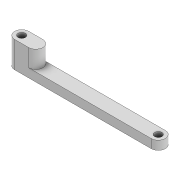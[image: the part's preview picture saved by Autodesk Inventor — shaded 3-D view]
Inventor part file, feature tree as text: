
AUTODESK INVENTOR PART (.ipt)
format: ipt  version: 2022 (Build 260153000, 153)  size: 117,248 bytes
history: native  units: mm
features: extrude x2, sketch x2, projected_geometry x1
ambient origin geometry x8: Origin, YZ Plane, XZ Plane, XY Plane, X Axis, Y Axis, Z Axis, Center Point
bodies: Solid1 (feature_tree)
feature tree (5):
  extrude  "Extrusion1"  Depth=8.0mm
  sketch  "Sketch2"  dims[d2=4.2mm d4=5.0mm d5=0.0mm d10=4.2mm d11=8.0mm d12=8.0mm d13=8.0mm d14=10.0mm d15=0.0mm]
  extrude  "Extrusion2"  Depth=5.0mm TaperAngle=0.0deg
  sketch  "Sketch1"  dims[d0=77.789mm d1=8.0mm]
  projected_geometry  "Projected Loop1"
